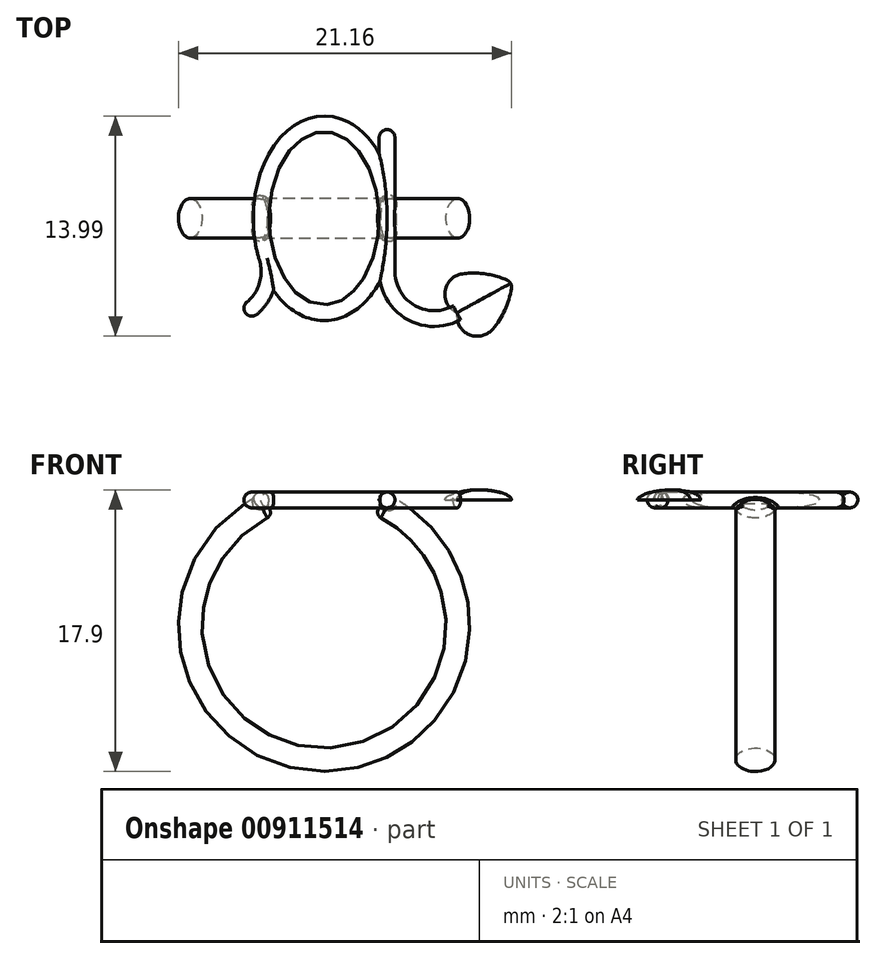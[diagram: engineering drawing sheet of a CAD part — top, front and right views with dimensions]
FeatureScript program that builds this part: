
annotation { "Feature Type Name" : "Feature", "Feature Type Description" : "" }
export const myFeature = defineFeature(function(context is Context, id is Id, definition is map)
    precondition{}
    {
        {
            var Q0;
            Q0=qCreatedBy(makeId("Right.planeOp"),FACE);
            var sketch = newSketch(context, id + "F0", { "sketchPlane" : qUnion([Q0])});
            skEllipse(sketch, "E0", {"center": v(0, -8.5) * mm, "majorRadius": 1.25 * mm, "minorRadius": 0.75 * mm, "majorAxis": v(1, 0)});
            skLineSegment(sketch, "E1", {"start": v(-8.37, 0) * mm, "end": v(10.93, 0) * mm, "construction": true});
            skSolve(sketch);
        }
        {
            var Q0;
            Q0=makeQuery(id+"F0.imprint","IMPRINT",FACE,{"disambiguationData":[TD([[makeQuery(id+"F0.imprint","IMPRINT",EDGE,{"derivedFrom":sQuery(id+"F0.wireOp",EDGE,"E0")}),1.0]])]});
            var Q1;
            Q1=sQuery(id+"F0.wireOp",EDGE,"E1");
            revolve(context, id + "F1", {"entities" : qUnion([Q0]), "axis" : qUnion([Q1]), "revolveType" : RevolveType.TWO_DIRECTIONS, "angle" : 155 * degree, "angleBack" : 205 * degree});
        }
        {
            var Q0;
            Q0=qCreatedBy(makeId("Top.planeOp"),FACE);
            cPlane(context, id + "F2", {"entities" : qUnion([Q0]), "cplaneType" : CPlaneType.OFFSET, "offset" : 8 * mm, "width" : 150 * mm, "height" : 150 * mm});
        }
        {
            var Q0;
            Q0=qCreatedBy(id+"F2.planeOp",FACE);
            var sketch = newSketch(context, id + "F3", { "sketchPlane" : qUnion([Q0])});
            skEllipse(sketch, "E2", {"center": v(0, 0) * mm, "majorRadius": 6 * mm, "minorRadius": 4 * mm, "majorAxis": v(0, 1)});
            skLineSegment(sketch, "E3", {"start": v(4, 5.63) * mm, "end": v(4, -3.37) * mm});
            skArc(sketch, "E4", {"start": v(4, -3.37) * mm, "mid": v(5.47, -5.95) * mm, "end": v(8.44, -6) * mm});
            skLineSegment(sketch, "E5", {"start": v(-7.83, -6) * mm, "end": v(11.12, -6) * mm, "construction": true});
            skArc(sketch, "E6", {"start": v(-5, -6) * mm, "mid": v(-3.7, -4.5) * mm, "end": v(-3.63, -2.52) * mm});
            skSolve(sketch);
        }
        {
            var Q0;
            Q0=sQuery(id+"F3.wireOp",VERTEX,"E3.start");
            var Q1;
            Q1=sQuery(id+"F3.wireOp",EDGE,"E3");
            cPlane(context, id + "F4", {"entities" : qUnion([Q0, Q1]), "cplaneType" : CPlaneType.LINE_POINT, "offset" : 150 * mm, "width" : 150 * mm, "height" : 150 * mm});
        }
        {
            var Q0;
            Q0=qCreatedBy(id+"F4.planeOp",FACE);
            var sketch = newSketch(context, id + "F5", { "sketchPlane" : qUnion([Q0])});
            skCircle(sketch, "E7", {"center": v(4, 8) * mm, "radius": 0.5 * mm});
            skSolve(sketch);
        }
        {
            var Q0;
            Q0=makeQuery(id+"F5.imprint","IMPRINT",FACE,{"disambiguationData":[TD([[makeQuery(id+"F5.imprint","IMPRINT",EDGE,{"derivedFrom":sQuery(id+"F5.wireOp",EDGE,"E7")}),1.0]])]});
            var Q1;
            Q1=sQuery(id+"F3.wireOp",EDGE,"E3");
            var Q2;
            Q2=sQuery(id+"F3.wireOp",EDGE,"E4");
            sweep(context, id + "F6", {"operationType" : NewBodyOperationType.ADD, "profiles" : qUnion([Q0]), "path" : qUnion([Q1, Q2])});
        }
        {
            var Q0;
            Q0=qCreatedBy(makeId("Right.planeOp"),FACE);
            var sketch = newSketch(context, id + "F7", { "sketchPlane" : qUnion([Q0])});
            skCircle(sketch, "E8", {"center": v(6, 8) * mm, "radius": 0.5 * mm});
            skLineSegment(sketch, "E9.0", {"start": v(-6, 8) * mm, "end": v(6, 8) * mm});
            skSolve(sketch);
        }
        {
            var Q0;
            Q0=makeQuery(id+"F7.imprint","IMPRINT",FACE,{"disambiguationData":[TD([[makeQuery(id+"F7.imprint","IMPRINT",EDGE,{"derivedFrom":sQuery(id+"F7.wireOp",EDGE,"E8")}),1.0]])]});
            var Q1;
            Q1=sQuery(id+"F3.wireOp",EDGE,"E2");
            sweep(context, id + "F8", {"operationType" : NewBodyOperationType.ADD, "profiles" : qUnion([Q0]), "path" : qUnion([Q1])});
        }
        {
            var Q0;
            Q0=sQuery(id+"F3.wireOp",VERTEX,"E6.start");
            var Q1;
            Q1=sQuery(id+"F3.wireOp",EDGE,"E6");
            cPlane(context, id + "F9", {"entities" : qUnion([Q0, Q1]), "cplaneType" : CPlaneType.CURVE_POINT, "offset" : 150 * mm, "width" : 150 * mm, "height" : 150 * mm});
        }
        {
            var Q0;
            Q0=qCreatedBy(id+"F9.planeOp",FACE);
            var sketch = newSketch(context, id + "F10", { "sketchPlane" : qUnion([Q0])});
            skCircle(sketch, "E10", {"center": v(-2.7, 8) * mm, "radius": 0.5 * mm});
            skSolve(sketch);
        }
        {
            var Q0;
            Q0=makeQuery(id+"F10.imprint","IMPRINT",FACE,{"disambiguationData":[TD([[makeQuery(id+"F10.imprint","IMPRINT",EDGE,{"derivedFrom":sQuery(id+"F10.wireOp",EDGE,"E10")}),1.0]])]});
            var Q1;
            Q1=sQuery(id+"F3.wireOp",EDGE,"E6");
            sweep(context, id + "F11", {"operationType" : NewBodyOperationType.ADD, "profiles" : qUnion([Q0]), "path" : qUnion([Q1])});
        }
        {
            var Q0;
            Q0=makeQuery(id+"F1.opRevolve","CAP_EDGE",EDGE,{"disambiguationData":[OSD([sQuery(id+"F0.wireOp",EDGE,"E0")])],"isStart":false});
            var Q1;
            Q1=makeQuery(id+"F1.opRevolve","CAP_EDGE",EDGE,{"disambiguationData":[OSD([sQuery(id+"F0.wireOp",EDGE,"E0")])],"isStart":true});
            fillet(context, id + "F12", {"entities" : qUnion([Q0, Q1]), "radius" : .4 * mm, "tangentPropagation" : true, "allowEdgeOverflow" : false});
        }
        {
            var Q0;
            Q0=makeQuery(id+"F6.opSweep","CAP_EDGE",EDGE,{"disambiguationData":[OSD([sQuery(id+"F3.wireOp",VERTEX,"E3.start"),sQuery(id+"F5.wireOp",EDGE,"E7")])],"isStart":true});
            var Q1;
            Q1=makeQuery(id+"F11.opSweep","CAP_EDGE",EDGE,{"disambiguationData":[OSD([sQuery(id+"F3.wireOp",VERTEX,"E6.start"),sQuery(id+"F10.wireOp",EDGE,"E10")])],"isStart":true});
            fillet(context, id + "F13", {"entities" : qUnion([Q0, Q1]), "radius" : .5 * mm, "tangentPropagation" : true, "allowEdgeOverflow" : false});
        }
        {
            var Q0;
            Q0=makeQuery(id+"F12.opFillet","BLEND_EDGE",EDGE,{"disambiguationData":[OD(0.0)],"blendedFrom":[makeQuery(id+"F1.opRevolve","CAP_EDGE",EDGE,{"disambiguationData":[OSD([sQuery(id+"F0.wireOp",EDGE,"E0")])],"isStart":true}),makeQuery(id+"F8.opSweep","SWEPT_FACE",FACE,{"disambiguationData":[OSD([sQuery(id+"F3.wireOp",EDGE,"E2"),sQuery(id+"F7.wireOp",EDGE,"E8")])]})],"blendedInto":[makeQuery(id+"F8.opSweep","SWEPT_FACE",FACE,{"disambiguationData":[OSD([sQuery(id+"F3.wireOp",EDGE,"E2"),sQuery(id+"F7.wireOp",EDGE,"E8")])]})]});
            var Q1;
            Q1=makeQuery(id+"F8.boolean.opBoolean","INTERSECT",EDGE,{"derivedFrom":[makeQuery(id+"F1.opRevolve","CAP_FACE",FACE,{"disambiguationData":[OSD([sQuery(id+"F0.wireOp",EDGE,"E0")])],"isStart":true}),makeQuery(id+"F8.opSweep","SWEPT_FACE",FACE,{"disambiguationData":[OSD([sQuery(id+"F3.wireOp",EDGE,"E2"),sQuery(id+"F7.wireOp",EDGE,"E8")])]})]});
            var Q2;
            Q2=makeQuery(id+"F6.boolean.opBoolean","INTERSECT",EDGE,{"derivedFrom":[makeQuery(id+"F1.opRevolve","SWEPT_FACE",FACE,{"disambiguationData":[OSD([sQuery(id+"F0.wireOp",EDGE,"E0")])]}),makeQuery(id+"F6.opSweep","SWEPT_FACE",FACE,{"disambiguationData":[OSD([sQuery(id+"F3.wireOp",EDGE,"E3"),sQuery(id+"F5.wireOp",EDGE,"E7")])]})]});
            var Q3;
            Q3=makeQuery(id+"F12.opFillet","BLEND_EDGE",EDGE,{"disambiguationData":[OD(1.0)],"blendedFrom":[makeQuery(id+"F1.opRevolve","CAP_EDGE",EDGE,{"disambiguationData":[OSD([sQuery(id+"F0.wireOp",EDGE,"E0")])],"isStart":true}),makeQuery(id+"F8.opSweep","SWEPT_FACE",FACE,{"disambiguationData":[OSD([sQuery(id+"F3.wireOp",EDGE,"E2"),sQuery(id+"F7.wireOp",EDGE,"E8")])]})],"blendedInto":[makeQuery(id+"F8.opSweep","SWEPT_FACE",FACE,{"disambiguationData":[OSD([sQuery(id+"F3.wireOp",EDGE,"E2"),sQuery(id+"F7.wireOp",EDGE,"E8")])]})]});
            var Q4;
            Q4=makeQuery(id+"F12.opFillet","BLEND_EDGE",EDGE,{"disambiguationData":[OD(1.0)],"blendedFrom":[makeQuery(id+"F1.opRevolve","CAP_EDGE",EDGE,{"disambiguationData":[OSD([sQuery(id+"F0.wireOp",EDGE,"E0")])],"isStart":false}),makeQuery(id+"F8.opSweep","SWEPT_FACE",FACE,{"disambiguationData":[OSD([sQuery(id+"F3.wireOp",EDGE,"E2"),sQuery(id+"F7.wireOp",EDGE,"E8")])]})],"blendedInto":[makeQuery(id+"F8.opSweep","SWEPT_FACE",FACE,{"disambiguationData":[OSD([sQuery(id+"F3.wireOp",EDGE,"E2"),sQuery(id+"F7.wireOp",EDGE,"E8")])]})]});
            var Q5;
            {var subQ0=sQuery(id+"F0.wireOp",EDGE,"E0");Q5=makeQuery(id+"F12.opFillet","BLEND_EDGE",EDGE,{"blendedFrom":[makeQuery(id+"F1.opRevolve","CAP_EDGE",EDGE,{"disambiguationData":[OSD([subQ0])],"isStart":false}),makeQuery(id+"F1.opRevolve","CAP_FACE",FACE,{"disambiguationData":[OSD([subQ0])],"isStart":false})],"blendedInto":[makeQuery(id+"F1.opRevolve","CAP_FACE",FACE,{"disambiguationData":[OSD([subQ0])],"isStart":false})]});}
            var Q6;
            Q6=makeQuery(id+"F8.boolean.opBoolean","INTERSECT",EDGE,{"disambiguationData":[OD(2.0)],"derivedFrom":[makeQuery(id+"F1.opRevolve","SWEPT_FACE",FACE,{"disambiguationData":[OSD([sQuery(id+"F0.wireOp",EDGE,"E0")])]}),makeQuery(id+"F8.opSweep","SWEPT_FACE",FACE,{"disambiguationData":[OSD([sQuery(id+"F3.wireOp",EDGE,"E2"),sQuery(id+"F7.wireOp",EDGE,"E8")])]})]});
            var Q7;
            Q7=makeQuery(id+"F12.opFillet","BLEND_EDGE",EDGE,{"disambiguationData":[OD(0.0)],"blendedFrom":[makeQuery(id+"F1.opRevolve","CAP_EDGE",EDGE,{"disambiguationData":[OSD([sQuery(id+"F0.wireOp",EDGE,"E0")])],"isStart":false}),makeQuery(id+"F8.opSweep","SWEPT_FACE",FACE,{"disambiguationData":[OSD([sQuery(id+"F3.wireOp",EDGE,"E2"),sQuery(id+"F7.wireOp",EDGE,"E8")])]})],"blendedInto":[makeQuery(id+"F8.opSweep","SWEPT_FACE",FACE,{"disambiguationData":[OSD([sQuery(id+"F3.wireOp",EDGE,"E2"),sQuery(id+"F7.wireOp",EDGE,"E8")])]})]});
            fillet(context, id + "F14", {"entities" : qUnion([Q0, Q1, Q2, Q3, Q4, Q5, Q6, Q7]), "radius" : .2 * mm, "tangentPropagation" : true, "allowEdgeOverflow" : false});
        }
        {
            var Q0;
            Q0=makeQuery(id+"F6.opSweep","CAP_FACE",FACE,{"disambiguationData":[OSD([sQuery(id+"F3.wireOp",VERTEX,"E4.end"),sQuery(id+"F5.wireOp",EDGE,"E7")])],"isStart":false});
            cPlane(context, id + "F15", {"entities" : qUnion([Q0]), "cplaneType" : CPlaneType.OFFSET, "offset" : 0 * mm, "width" : 150 * mm, "height" : 150 * mm});
        }
        {
            var Q0;
            Q0=qCreatedBy(id+"F15.planeOp",FACE);
            cPlane(context, id + "F16", {"entities" : qUnion([Q0]), "cplaneType" : CPlaneType.OFFSET, "offset" : 1.5 * mm, "width" : 150 * mm, "height" : 150 * mm});
        }
        {
            var Q0;
            Q0=qCreatedBy(id+"F16.planeOp",FACE);
            cPlane(context, id + "F17", {"entities" : qUnion([Q0]), "cplaneType" : CPlaneType.OFFSET, "offset" : 2.5 * mm, "width" : 150 * mm, "height" : 150 * mm});
        }
        {
            var Q0;
            Q0=qCreatedBy(id+"F15.planeOp",FACE);
            var sketch = newSketch(context, id + "F18", { "sketchPlane" : qUnion([Q0])});
            skPoint(sketch, "E11", {"position": v(-9.32, 8) * mm});
            skCircle(sketch, "E12.0.0", {"center": v(-9.32, 8) * mm, "radius": 0.5 * mm});
            skSolve(sketch);
        }
        {
            var Q0;
            Q0=qCreatedBy(id+"F16.planeOp",FACE);
            var sketch = newSketch(context, id + "F19", { "sketchPlane" : qUnion([Q0])});
            skEllipse(sketch, "E13", {"center": v(-9.32, 8) * mm, "majorRadius": 2 * mm, "minorRadius": 0.65 * mm, "majorAxis": v(1, 0)});
            skLineSegment(sketch, "E14", {"start": v(-7.32, 9.11) * mm, "end": v(-7.32, 6.5) * mm, "construction": true});
            skLineSegment(sketch, "E15", {"start": v(-11.32, 9.41) * mm, "end": v(-11.32, 7.2) * mm, "construction": true});
            skSolve(sketch);
        }
        {
            var Q0;
            Q0=qCreatedBy(id+"F17.planeOp",FACE);
            var sketch = newSketch(context, id + "F20", { "sketchPlane" : qUnion([Q0])});
            skPoint(sketch, "E16", {"position": v(-9.32, 8) * mm});
            skSolve(sketch);
        }
        {
            var Q0;
            Q0=qCreatedBy(id+"F2.planeOp",FACE);
            var sketch = newSketch(context, id + "F21", { "sketchPlane" : qUnion([Q0])});
            skArc(sketch, "E17", {"start": v(8.8, -3.53) * mm, "mid": v(7.68, -4.63) * mm, "end": v(8.44, -6) * mm, "construction": true});
            skArc(sketch, "E18", {"start": v(8.8, -3.53) * mm, "mid": v(10.23, -3.53) * mm, "end": v(11.6, -3.92) * mm, "construction": true});
            skPoint(sketch, "E19", {"position": v(8.8, -3.53) * mm});
            skLineSegment(sketch, "E20", {"start": v(8.44, -6) * mm, "end": v(11.95, -4.08) * mm, "construction": true});
            skArc(sketch, "E21.MirrorCS", {"start": v(10.72, -7.03) * mm, "mid": v(11.49, -5.83) * mm, "end": v(11.9, -4.45) * mm});
            skArc(sketch, "E22.MirrorCS", {"start": v(10.72, -7.03) * mm, "mid": v(9.19, -7.38) * mm, "end": v(8.44, -6) * mm});
            skPoint(sketch, "E23.visualSharp", {"position": v(11.95, -4.08) * mm});
            skArc(sketch, "E23.filletArc", {"start": v(11.9, -4.45) * mm, "mid": v(11.9, -4.29) * mm, "end": v(11.85, -4.13) * mm});
            skArc(sketch, "E24", {"start": v(11.85, -4.13) * mm, "mid": v(11.75, -4) * mm, "end": v(11.6, -3.92) * mm, "construction": true});
            skLineSegment(sketch, "E25", {"start": v(8.8, -3.53) * mm, "end": v(9.76, -5.28) * mm, "construction": true});
            skSolve(sketch);
        }
        {
            var Q0;
            Q0=sQuery(id+"F21.wireOp",EDGE,"E20");
            cPlane(context, id + "F22", {"entities" : qUnion([Q0]), "cplaneType" : CPlaneType.LINE_ANGLE, "offset" : 150 * mm, "angle" : 0 * degree, "width" : 150 * mm, "height" : 150 * mm});
        }
        {
            var Q0;
            Q0=qCreatedBy(id+"F22.planeOp",FACE);
            var sketch = newSketch(context, id + "F23", { "sketchPlane" : qUnion([Q0])});
            skLineSegment(sketch, "E26", {"start": v(-6.02, 8) * mm, "end": v(-6.02, 8.65) * mm});
            skLineSegment(sketch, "E27", {"start": v(-6.02, 8) * mm, "end": v(-8.4, 8) * mm});
            skEllipticalArc(sketch, "E28", {});
            const initialGuessF23  = {"E28": [-0.006023315396989856, 0.008, -1, 0, 0.0023850018281689226, 0.00065, 4.71238898038469, 0]};
            skSetInitialGuess(sketch, initialGuessF23);
            skSolve(sketch);
        }
        {
            var Q0;
            Q0=qCreatedBy(id+"F16.planeOp",FACE);
            var sketch = newSketch(context, id + "F24", { "sketchPlane" : qUnion([Q0])});
            skLineSegment(sketch, "E29.0", {"start": v(-9.32, 8) * mm, "end": v(-9.32, 8.65) * mm});
            skLineSegment(sketch, "E30", {"start": v(-9.32, 8) * mm, "end": v(-11.32, 8) * mm});
            skEllipticalArc(sketch, "E31.0", {});
            const initialGuessF24  = {"E31.0": [-0.009315497004728895, 0.008, 1, 0, 0.002, 0.00065, 1.5707963267948974, 3.141592653589793]};
            skSetInitialGuess(sketch, initialGuessF24);
            skSolve(sketch);
        }
        {
            var Q0;
            Q0=qCreatedBy(id+"F22.planeOp",FACE);
            var sketch = newSketch(context, id + "F25", { "sketchPlane" : qUnion([Q0])});
            skLineSegment(sketch, "E32.0", {"start": v(-4.52, 8) * mm, "end": v(-6.02, 8) * mm});
            skLineSegment(sketch, "E32.1", {"start": v(-6.02, 8) * mm, "end": v(-6.02, 8.65) * mm});
            skPoint(sketch, "E33.orphan", {"position": v(-8.52, 8) * mm});
            skEllipticalArc(sketch, "E34", {});
            const initialGuessF25  = {"E34": [-0.006023315396989857, 0.008, 1, 0, 0.0015, 0.00065, 0, 1.5707963267948972]};
            skSetInitialGuess(sketch, initialGuessF25);
            skSolve(sketch);
        }
        {
            var Q0;
            Q0=qSketchRegion(id+"F23",true);
            var Q1;
            Q1=qSketchRegion(id+"F24",true);
            var Q2;
            Q2=qSketchRegion(id+"F25",true);
            var Q3;
            Q3=qConstructionFilter(qBodyType(qCreatedBy(id+"F21",EDGE),BodyType.WIRE),ConstructionObject.NO);
            loft(context, id + "F26", {"addGuides" : true, "sheetProfilesArray" : [{ "sheetProfileEntities" : qUnion([Q0]) }, { "sheetProfileEntities" : qUnion([Q1]) }, { "sheetProfileEntities" : qUnion([Q2]) }], "guidesArray" : [{ "guideEntities" : qUnion([Q3]), "guideDerivativeType" : LoftGuideDerivativeType.DEFAULT, "guideDerivativeMagnitude" : 1 }]});
        }
        {
            var Q0;
            Q0=makeQuery(id+"F26.opLoft","SWEPT_BODY",BODY,{"disambiguationData":[OSD([sQuery(id+"F21.wireOp",EDGE,"E22.MirrorCS"),makeQuery(id+"F23.imprint","IMPRINT",FACE,{"disambiguationData":[TD([[makeQuery(id+"F23.imprint","IMPRINT",EDGE,{"derivedFrom":sQuery(id+"F23.wireOp",EDGE,"E26")}),1.0]])]}),sQuery(id+"F24.wireOp",EDGE,"E29.0"),makeQuery(id+"F25.imprint","IMPRINT",FACE,{"disambiguationData":[TD([[makeQuery(id+"F25.imprint","IMPRINT",EDGE,{"derivedFrom":sQuery(id+"F25.wireOp",EDGE,"E32.0")}),-1.0]])]})])]});
            var Q1;
            Q1=qCreatedBy(id+"F22.planeOp",FACE);
            mirror(context, id + "F27", {"entities" : qUnion([Q0]), "mirrorPlane" : qUnion([Q1])});
        }
    });
